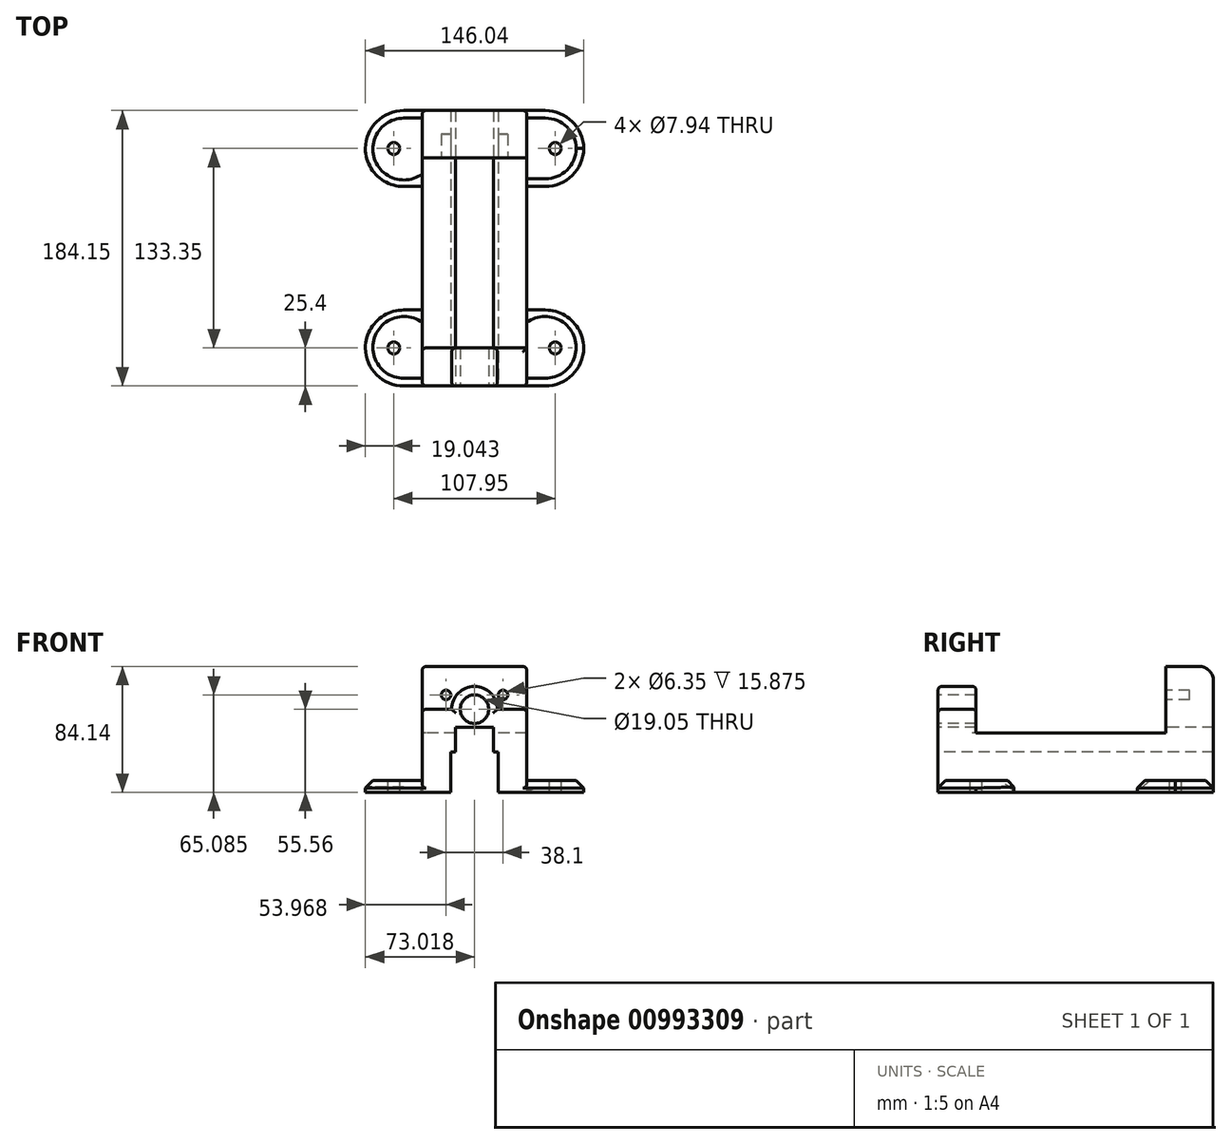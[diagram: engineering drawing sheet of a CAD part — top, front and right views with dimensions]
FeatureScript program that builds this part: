
annotation { "Feature Type Name" : "Feature", "Feature Type Description" : "" }
export const myFeature = defineFeature(function(context is Context, id is Id, definition is map)
    precondition{}
    {
        {
            var Q0;
            Q0=qCreatedBy(makeId("Front.planeOp"),FACE);
            var sketch = newSketch(context, id + "F0", { "sketchPlane" : qUnion([Q0])});
            skLineSegment(sketch, "E0", {"start": v(-29.15, 0) * mm, "end": v(40.7, 0) * mm});
            skLineSegment(sketch, "E1", {"start": v(40.7, 0) * mm, "end": v(40.7, -55.56) * mm});
            skLineSegment(sketch, "E2", {"start": v(40.7, -55.56) * mm, "end": v(-29.15, -55.56) * mm});
            skLineSegment(sketch, "E3", {"start": v(-29.15, -55.56) * mm, "end": v(-29.15, 0) * mm});
            skSolve(sketch);
        }
        {
            var Q0;
            Q0=makeQuery(id+"F0.imprint","IMPRINT",FACE,{"disambiguationData":[TD([[makeQuery(id+"F0.imprint","IMPRINT",EDGE,{"derivedFrom":sQuery(id+"F0.wireOp",EDGE,"E0")}),-1.0]])]});
            extrude(context, id + "F1", {"entities" : qUnion([Q0]), "depth" : 25.4 * mm, "offsetDistance" : 25.4 * mm});
        }
        {
            var Q0;
            Q0=makeQuery(id+"F1.opExtrude","CAP_FACE",FACE,{"disambiguationData":[OSD([sQuery(id+"F0.wireOp",EDGE,"E0"),sQuery(id+"F0.wireOp",EDGE,"E1"),sQuery(id+"F0.wireOp",EDGE,"E2"),sQuery(id+"F0.wireOp",EDGE,"E3")])],"isStart":false});
            var sketch = newSketch(context, id + "F2", { "sketchPlane" : qUnion([Q0])});
            skCircle(sketch, "E4", {"center": v(5.78, 0) * mm, "radius": 15.24 * mm});
            skSolve(sketch);
        }
        {
            var Q0;
            {var subQ0=sQuery(id+"F2.wireOp",EDGE,"E4");var subQ1=makeQuery(id+"F1.opExtrude","CAP_EDGE",EDGE,{"disambiguationData":[OSD([sQuery(id+"F0.wireOp",EDGE,"E0")])],"isStart":false});var subQ2=makeQuery(id+"F2.imprint","INTERSECT",VERTEX,{"disambiguationData":[OD(0.0)],"derivedFrom":[subQ1,subQ0]});Q0=makeQuery(id+"F2.imprint","IMPRINT",FACE,{"disambiguationData":[TD([[makeQuery(id+"F2.imprint","IMPRINT",EDGE,{"disambiguationData":[TD([[subQ2,1.0]])],"derivedFrom":subQ0}),1.0]])]});}
            extrude(context, id + "F3", {"entities" : qUnion([Q0]), "operationType" : NewBodyOperationType.ADD, "oppositeDirection" : true, "depth" : 25.4 * mm, "offsetDistance" : 25.4 * mm});
        }
        {
            var Q0;
            {var subQ0=sQuery(id+"F0.wireOp",EDGE,"E0");Q0=makeQuery(id+"F3.boolean.opBoolean","MERGE",FACE,{"derivedFrom":[makeQuery(id+"F1.opExtrude","CAP_FACE",FACE,{"disambiguationData":[OSD([subQ0,sQuery(id+"F0.wireOp",EDGE,"E1"),sQuery(id+"F0.wireOp",EDGE,"E2"),sQuery(id+"F0.wireOp",EDGE,"E3")])],"isStart":false}),makeQuery(id+"F3.opExtrude","CAP_FACE",FACE,{"disambiguationData":[OSD([subQ0,sQuery(id+"F2.wireOp",EDGE,"E4")])],"isStart":true})]});}
            var sketch = newSketch(context, id + "F4", { "sketchPlane" : qUnion([Q0])});
            skCircle(sketch, "E5", {"center": v(5.78, 0) * mm, "radius": 7.94 * mm});
            skSolve(sketch);
        }
        {
            var Q0;
            Q0=makeQuery(id+"F4.imprint","IMPRINT",FACE,{"disambiguationData":[TD([[makeQuery(id+"F4.imprint","IMPRINT",EDGE,{"derivedFrom":sQuery(id+"F4.wireOp",EDGE,"E5")}),1.0]])]});
            extrude(context, id + "F5", {"entities" : qUnion([Q0]), "operationType" : NewBodyOperationType.REMOVE, "oppositeDirection" : true, "depth" : 25.4 * mm, "offsetDistance" : 25.4 * mm});
        }
        {
            var Q0;
            {var subQ0=sQuery(id+"F0.wireOp",EDGE,"E0");Q0=makeQuery(id+"F3.boolean.opBoolean","MERGE",FACE,{"derivedFrom":[makeQuery(id+"F1.opExtrude","CAP_FACE",FACE,{"disambiguationData":[OSD([subQ0,sQuery(id+"F0.wireOp",EDGE,"E1"),sQuery(id+"F0.wireOp",EDGE,"E2"),sQuery(id+"F0.wireOp",EDGE,"E3")])],"isStart":true}),makeQuery(id+"F3.opExtrude","CAP_FACE",FACE,{"disambiguationData":[OSD([subQ0,sQuery(id+"F2.wireOp",EDGE,"E4")])],"isStart":false})]});}
            var sketch = newSketch(context, id + "F6", { "sketchPlane" : qUnion([Q0])});
            skLineSegment(sketch, "E6", {"start": v(-40.7, -55.56) * mm, "end": v(-40.7, -15.88) * mm});
            skLineSegment(sketch, "E7", {"start": v(-40.7, -15.88) * mm, "end": v(29.15, -15.88) * mm});
            skLineSegment(sketch, "E8", {"start": v(29.15, -15.88) * mm, "end": v(29.15, -55.56) * mm});
            skLineSegment(sketch, "E9", {"start": v(29.15, -55.56) * mm, "end": v(-40.7, -55.56) * mm});
            skSolve(sketch);
        }
        {
            var Q0;
            Q0=makeQuery(id+"F6.imprint","IMPRINT",FACE,{"disambiguationData":[TD([[makeQuery(id+"F6.imprint","IMPRINT",EDGE,{"derivedFrom":sQuery(id+"F6.wireOp",EDGE,"E6")}),1.0]])]});
            extrude(context, id + "F7", {"entities" : qUnion([Q0]), "operationType" : NewBodyOperationType.ADD, "depth" : 127 * mm, "offsetDistance" : 25.4 * mm});
        }
        {
            var Q0;
            Q0=makeQuery(id+"F7.opExtrude","CAP_FACE",FACE,{"disambiguationData":[OSD([sQuery(id+"F6.wireOp",EDGE,"E6"),sQuery(id+"F6.wireOp",EDGE,"E7"),sQuery(id+"F6.wireOp",EDGE,"E8"),sQuery(id+"F6.wireOp",EDGE,"E9")])],"isStart":false});
            var sketch = newSketch(context, id + "F8", { "sketchPlane" : qUnion([Q0])});
            skLineSegment(sketch, "E10", {"start": v(-40.7, -15.88) * mm, "end": v(-40.7, 28.57) * mm});
            skLineSegment(sketch, "E11", {"start": v(-40.7, 28.57) * mm, "end": v(29.15, 28.57) * mm});
            skLineSegment(sketch, "E12", {"start": v(29.15, 28.57) * mm, "end": v(29.15, -15.88) * mm});
            skLineSegment(sketch, "E13", {"start": v(29.15, -15.88) * mm, "end": v(-40.7, -15.88) * mm});
            skSolve(sketch);
        }
        {
            var Q0;
            Q0=makeQuery(id+"F8.imprint","IMPRINT",FACE,{"disambiguationData":[TD([[makeQuery(id+"F8.imprint","IMPRINT",EDGE,{"derivedFrom":sQuery(id+"F8.wireOp",EDGE,"E10")}),-1.0]])]});
            var Q1;
            Q1=makeQuery(id+"F8.imprint","IMPRINT",FACE,{"disambiguationData":[TD([[makeQuery(id+"F8.imprint","IMPRINT",EDGE,{"derivedFrom":sQuery(id+"F8.wireOp",EDGE,"E13")}),-1.0]])]});
            extrude(context, id + "F9", {"entities" : qUnion([Q0, Q1]), "operationType" : NewBodyOperationType.ADD, "depth" : 31.75 * mm, "offsetDistance" : 25.4 * mm});
        }
        {
            var Q0;
            Q0=makeQuery(id+"F9.opExtrude","CAP_EDGE",EDGE,{"disambiguationData":[OSD([sQuery(id+"F8.wireOp",EDGE,"E11")])],"isStart":false});
            fillet(context, id + "F10", {"entities" : qUnion([Q0]), "radius" : 9.52 * mm, "tangentPropagation" : true, "allowEdgeOverflow" : false});
        }
        {
            var Q0;
            {var subQ0=sQuery(id+"F0.wireOp",EDGE,"E0");Q0=makeQuery(id+"F3.boolean.opBoolean","MERGE",FACE,{"derivedFrom":[makeQuery(id+"F1.opExtrude","CAP_FACE",FACE,{"disambiguationData":[OSD([subQ0,sQuery(id+"F0.wireOp",EDGE,"E1"),sQuery(id+"F0.wireOp",EDGE,"E2"),sQuery(id+"F0.wireOp",EDGE,"E3")])],"isStart":false}),makeQuery(id+"F3.opExtrude","CAP_FACE",FACE,{"disambiguationData":[OSD([subQ0,sQuery(id+"F2.wireOp",EDGE,"E4")])],"isStart":true})]});}
            var sketch = newSketch(context, id + "F11", { "sketchPlane" : qUnion([Q0])});
            skLineSegment(sketch, "E14", {"start": v(5.78, -55.56) * mm, "end": v(-10.16, -55.56) * mm});
            skLineSegment(sketch, "E15", {"start": v(-10.16, -55.56) * mm, "end": v(21.72, -55.56) * mm});
            skLineSegment(sketch, "E16", {"start": v(21.72, -55.56) * mm, "end": v(21.72, -28.58) * mm});
            skLineSegment(sketch, "E17", {"start": v(-10.16, -55.56) * mm, "end": v(-10.16, -28.58) * mm});
            skLineSegment(sketch, "E18", {"start": v(-10.16, -28.58) * mm, "end": v(21.72, -28.58) * mm});
            skLineSegment(sketch, "E19", {"start": v(5.78, -28.58) * mm, "end": v(-6.97, -28.58) * mm});
            skLineSegment(sketch, "E20", {"start": v(-6.97, -28.58) * mm, "end": v(18.53, -28.58) * mm});
            skLineSegment(sketch, "E21", {"start": v(18.53, -28.58) * mm, "end": v(18.53, -15.82) * mm});
            skLineSegment(sketch, "E22", {"start": v(-6.97, -28.58) * mm, "end": v(-6.97, -15.82) * mm});
            skLineSegment(sketch, "E23", {"start": v(-6.97, -15.82) * mm, "end": v(18.53, -15.82) * mm});
            skSolve(sketch);
        }
        {
            var Q0;
            {var subQ1=sQuery(id+"F11.wireOp",EDGE,"E21");Q0=makeQuery(id+"F11.imprint","IMPRINT",FACE,{"disambiguationData":[TD([[makeQuery(id+"F11.imprint","IMPRINT",EDGE,{"derivedFrom":subQ1}),1.0]])]});}
            var Q1;
            {var subQ4=sQuery(id+"F11.wireOp",EDGE,"E16");Q1=makeQuery(id+"F11.imprint","IMPRINT",FACE,{"disambiguationData":[TD([[makeQuery(id+"F11.imprint","IMPRINT",EDGE,{"derivedFrom":subQ4}),1.0]])]});}
            extrude(context, id + "F12", {"entities" : qUnion([Q0, Q1]), "operationType" : NewBodyOperationType.REMOVE, "oppositeDirection" : true, "depth" : 210.06 * mm, "offsetDistance" : 25.4 * mm});
        }
        {
            var Q0;
            {var subQ0=sQuery(id+"F0.wireOp",EDGE,"E0");Q0=makeQuery(id+"F3.boolean.opBoolean","MERGE",FACE,{"derivedFrom":[makeQuery(id+"F1.opExtrude","CAP_FACE",FACE,{"disambiguationData":[OSD([subQ0,sQuery(id+"F0.wireOp",EDGE,"E1"),sQuery(id+"F0.wireOp",EDGE,"E2"),sQuery(id+"F0.wireOp",EDGE,"E3")])],"isStart":false}),makeQuery(id+"F3.opExtrude","CAP_FACE",FACE,{"disambiguationData":[OSD([subQ0,sQuery(id+"F2.wireOp",EDGE,"E4")])],"isStart":true})]});}
            var sketch = newSketch(context, id + "F13", { "sketchPlane" : qUnion([Q0])});
            skLineSegment(sketch, "E24", {"start": v(-6.97, -15.82) * mm, "end": v(-6.97, -12.01) * mm});
            skLineSegment(sketch, "E25", {"start": v(-6.97, -12.01) * mm, "end": v(18.53, -12.01) * mm});
            skLineSegment(sketch, "E26", {"start": v(18.53, -12.01) * mm, "end": v(18.53, -15.82) * mm});
            skSolve(sketch);
        }
        {
            var Q0;
            Q0=makeQuery(id+"F13.imprint","IMPRINT",FACE,{"disambiguationData":[TD([[makeQuery(id+"F13.imprint","IMPRINT",EDGE,{"derivedFrom":sQuery(id+"F13.wireOp",EDGE,"E24")}),-1.0]])]});
            extrude(context, id + "F14", {"entities" : qUnion([Q0]), "operationType" : NewBodyOperationType.REMOVE, "oppositeDirection" : true, "depth" : 222 * mm, "offsetDistance" : 25.4 * mm});
        }
        {
            var Q0;
            Q0=makeQuery(id+"F9.opExtrude","CAP_FACE",FACE,{"disambiguationData":[OSD([sQuery(id+"F6.wireOp",EDGE,"E6"),sQuery(id+"F6.wireOp",EDGE,"E8"),sQuery(id+"F6.wireOp",EDGE,"E9"),sQuery(id+"F8.wireOp",EDGE,"E10"),sQuery(id+"F8.wireOp",EDGE,"E11"),sQuery(id+"F8.wireOp",EDGE,"E12")])],"isStart":true});
            var sketch = newSketch(context, id + "F15", { "sketchPlane" : qUnion([Q0])});
            skLineSegment(sketch, "E27", {"start": v(-29.15, 28.57) * mm, "end": v(-29.15, 9.52) * mm});
            skLineSegment(sketch, "E28", {"start": v(-29.15, 9.52) * mm, "end": v(-13.27, 9.52) * mm});
            skCircle(sketch, "E29", {"center": v(-13.27, 9.52) * mm, "radius": 3.18 * mm});
            skLineSegment(sketch, "E30", {"start": v(40.7, 28.57) * mm, "end": v(40.7, 9.52) * mm});
            skLineSegment(sketch, "E31", {"start": v(40.7, 9.52) * mm, "end": v(24.83, 9.52) * mm});
            skCircle(sketch, "E32", {"center": v(24.83, 9.52) * mm, "radius": 3.18 * mm});
            skSolve(sketch);
        }
        {
            var Q0;
            Q0=makeQuery(id+"F15.imprint","IMPRINT",FACE,{"disambiguationData":[TD([[makeQuery(id+"F15.imprint","IMPRINT",EDGE,{"derivedFrom":sQuery(id+"F15.wireOp",EDGE,"E29")}),1.0]])]});
            var Q1;
            Q1=makeQuery(id+"F15.imprint","IMPRINT",FACE,{"disambiguationData":[TD([[makeQuery(id+"F15.imprint","IMPRINT",EDGE,{"derivedFrom":sQuery(id+"F15.wireOp",EDGE,"E32")}),1.0]])]});
            extrude(context, id + "F16", {"entities" : qUnion([Q0, Q1]), "operationType" : NewBodyOperationType.REMOVE, "oppositeDirection" : true, "depth" : 15.88 * mm, "offsetDistance" : 25.4 * mm});
        }
        {
            var Q0;
            {var subQ0=sQuery(id+"F6.wireOp",EDGE,"E6");Q0=makeQuery(id+"F9.boolean.opBoolean","MERGE",FACE,{"derivedFrom":[makeQuery(id+"F7.boolean.opBoolean","MERGE",FACE,{"derivedFrom":[makeQuery(id+"F1.opExtrude","SWEPT_FACE",FACE,{"disambiguationData":[OSD([sQuery(id+"F0.wireOp",EDGE,"E1")])]}),makeQuery(id+"F7.opExtrude","SWEPT_FACE",FACE,{"disambiguationData":[OSD([subQ0])]})]}),makeQuery(id+"F9.opExtrude","SWEPT_FACE",FACE,{"disambiguationData":[OSD([subQ0,sQuery(id+"F8.wireOp",EDGE,"E10")])]})]});}
            var sketch = newSketch(context, id + "F17", { "sketchPlane" : qUnion([Q0])});
            skLineSegment(sketch, "E33", {"start": v(-25.4, -55.56) * mm, "end": v(-25.4, -47.63) * mm});
            skLineSegment(sketch, "E34", {"start": v(-25.4, -47.63) * mm, "end": v(25.4, -47.63) * mm});
            skLineSegment(sketch, "E35", {"start": v(25.4, -47.63) * mm, "end": v(25.4, -55.56) * mm});
            skLineSegment(sketch, "E36", {"start": v(25.4, -55.56) * mm, "end": v(-25.4, -55.56) * mm});
            skLineSegment(sketch, "E37", {"start": v(158.75, -55.56) * mm, "end": v(158.75, -47.63) * mm});
            skLineSegment(sketch, "E38", {"start": v(158.75, -47.63) * mm, "end": v(107.95, -47.63) * mm});
            skLineSegment(sketch, "E39", {"start": v(107.95, -47.63) * mm, "end": v(107.95, -55.56) * mm});
            skLineSegment(sketch, "E40", {"start": v(107.95, -55.56) * mm, "end": v(158.75, -55.56) * mm});
            skSolve(sketch);
        }
        {
            var Q0;
            Q0=makeQuery(id+"F17.imprint","IMPRINT",FACE,{"disambiguationData":[TD([[makeQuery(id+"F17.imprint","IMPRINT",EDGE,{"derivedFrom":sQuery(id+"F17.wireOp",EDGE,"E33")}),1.0]])]});
            var Q1;
            Q1=makeQuery(id+"F17.imprint","IMPRINT",FACE,{"disambiguationData":[TD([[makeQuery(id+"F17.imprint","IMPRINT",EDGE,{"derivedFrom":sQuery(id+"F17.wireOp",EDGE,"E37")}),1.0]])]});
            extrude(context, id + "F18", {"entities" : qUnion([Q0, Q1]), "operationType" : NewBodyOperationType.ADD, "depth" : 38.1 * mm, "offsetDistance" : 25.4 * mm});
        }
        {
            var Q0;
            {var subQ0=sQuery(id+"F6.wireOp",EDGE,"E8");Q0=makeQuery(id+"F9.boolean.opBoolean","MERGE",FACE,{"derivedFrom":[makeQuery(id+"F7.boolean.opBoolean","MERGE",FACE,{"derivedFrom":[makeQuery(id+"F1.opExtrude","SWEPT_FACE",FACE,{"disambiguationData":[OSD([sQuery(id+"F0.wireOp",EDGE,"E3")])]}),makeQuery(id+"F7.opExtrude","SWEPT_FACE",FACE,{"disambiguationData":[OSD([subQ0])]})]}),makeQuery(id+"F9.opExtrude","SWEPT_FACE",FACE,{"disambiguationData":[OSD([subQ0,sQuery(id+"F8.wireOp",EDGE,"E12")])]})]});}
            var sketch = newSketch(context, id + "F19", { "sketchPlane" : qUnion([Q0])});
            skLineSegment(sketch, "E41", {"start": v(25.4, -55.56) * mm, "end": v(25.4, -47.63) * mm});
            skLineSegment(sketch, "E42", {"start": v(25.4, -47.63) * mm, "end": v(-25.4, -47.63) * mm});
            skLineSegment(sketch, "E43", {"start": v(-25.4, -47.63) * mm, "end": v(-25.4, -55.56) * mm});
            skLineSegment(sketch, "E44", {"start": v(-25.4, -55.56) * mm, "end": v(25.4, -55.56) * mm});
            skLineSegment(sketch, "E45", {"start": v(-158.75, -55.56) * mm, "end": v(-158.75, -47.63) * mm});
            skLineSegment(sketch, "E46", {"start": v(-158.75, -47.63) * mm, "end": v(-107.95, -47.63) * mm});
            skLineSegment(sketch, "E47", {"start": v(-107.95, -47.63) * mm, "end": v(-107.95, -55.56) * mm});
            skLineSegment(sketch, "E48", {"start": v(-107.95, -55.56) * mm, "end": v(-158.75, -55.56) * mm});
            skSolve(sketch);
        }
        {
            var Q0;
            Q0=makeQuery(id+"F19.imprint","IMPRINT",FACE,{"disambiguationData":[TD([[makeQuery(id+"F19.imprint","IMPRINT",EDGE,{"derivedFrom":sQuery(id+"F19.wireOp",EDGE,"E45")}),1.0]])]});
            var Q1;
            Q1=makeQuery(id+"F19.imprint","IMPRINT",FACE,{"disambiguationData":[TD([[makeQuery(id+"F19.imprint","IMPRINT",EDGE,{"derivedFrom":sQuery(id+"F19.wireOp",EDGE,"E41")}),1.0]])]});
            extrude(context, id + "F20", {"entities" : qUnion([Q0, Q1]), "operationType" : NewBodyOperationType.ADD, "depth" : 38.1 * mm, "offsetDistance" : 25.4 * mm});
        }
        {
            var Q0;
            Q0=makeQuery(id+"F18.opExtrude","SWEPT_FACE",FACE,{"disambiguationData":[OSD([sQuery(id+"F17.wireOp",EDGE,"E34")])]});
            var sketch = newSketch(context, id + "F21", { "sketchPlane" : qUnion([Q0])});
            skLineSegment(sketch, "E49", {"start": v(59.75, -25.4) * mm, "end": v(59.75, 0) * mm});
            skCircle(sketch, "E50", {"center": v(59.75, 0) * mm, "radius": 3.97 * mm});
            skSolve(sketch);
        }
        {
            var Q0;
            Q0=makeQuery(id+"F18.opExtrude","SWEPT_FACE",FACE,{"disambiguationData":[OSD([sQuery(id+"F17.wireOp",EDGE,"E38")])]});
            var sketch = newSketch(context, id + "F22", { "sketchPlane" : qUnion([Q0])});
            skLineSegment(sketch, "E51", {"start": v(59.75, 107.95) * mm, "end": v(59.75, 133.35) * mm});
            skCircle(sketch, "E52", {"center": v(59.75, 133.35) * mm, "radius": 3.97 * mm});
            skSolve(sketch);
        }
        {
            var Q0;
            Q0=makeQuery(id+"F20.opExtrude","SWEPT_FACE",FACE,{"disambiguationData":[OSD([sQuery(id+"F19.wireOp",EDGE,"E46")])]});
            var sketch = newSketch(context, id + "F23", { "sketchPlane" : qUnion([Q0])});
            skLineSegment(sketch, "E53", {"start": v(-48.2, 107.95) * mm, "end": v(-48.2, 133.35) * mm});
            skCircle(sketch, "E54", {"center": v(-48.2, 133.35) * mm, "radius": 3.97 * mm});
            skSolve(sketch);
        }
        {
            var Q0;
            Q0=makeQuery(id+"F20.opExtrude","SWEPT_FACE",FACE,{"disambiguationData":[OSD([sQuery(id+"F19.wireOp",EDGE,"E42")])]});
            var sketch = newSketch(context, id + "F24", { "sketchPlane" : qUnion([Q0])});
            skLineSegment(sketch, "E55", {"start": v(-48.2, 25.4) * mm, "end": v(-48.2, 0) * mm});
            skCircle(sketch, "E56", {"center": v(-48.2, 0) * mm, "radius": 3.97 * mm});
            skSolve(sketch);
        }
        {
            var Q0;
            Q0=makeQuery(id+"F23.imprint","IMPRINT",FACE,{"disambiguationData":[TD([[makeQuery(id+"F23.imprint","IMPRINT",EDGE,{"derivedFrom":sQuery(id+"F23.wireOp",EDGE,"E54")}),1.0]])]});
            var Q1;
            Q1=makeQuery(id+"F22.imprint","IMPRINT",FACE,{"disambiguationData":[TD([[makeQuery(id+"F22.imprint","IMPRINT",EDGE,{"derivedFrom":sQuery(id+"F22.wireOp",EDGE,"E52")}),1.0]])]});
            var Q2;
            Q2=makeQuery(id+"F21.imprint","IMPRINT",FACE,{"disambiguationData":[TD([[makeQuery(id+"F21.imprint","IMPRINT",EDGE,{"derivedFrom":sQuery(id+"F21.wireOp",EDGE,"E50")}),1.0]])]});
            var Q3;
            Q3=makeQuery(id+"F24.imprint","IMPRINT",FACE,{"disambiguationData":[TD([[makeQuery(id+"F24.imprint","IMPRINT",EDGE,{"derivedFrom":sQuery(id+"F24.wireOp",EDGE,"E56")}),1.0]])]});
            extrude(context, id + "F25", {"entities" : qUnion([Q0, Q1, Q2, Q3]), "operationType" : NewBodyOperationType.REMOVE, "oppositeDirection" : true, "depth" : 25.4 * mm, "offsetDistance" : 25.4 * mm});
        }
        {
            var Q0;
            Q0=makeQuery(id+"F18.opExtrude","CAP_EDGE",EDGE,{"disambiguationData":[OSD([sQuery(id+"F17.wireOp",EDGE,"E33")])],"isStart":false});
            var Q1;
            Q1=makeQuery(id+"F18.opExtrude","CAP_EDGE",EDGE,{"disambiguationData":[OSD([sQuery(id+"F17.wireOp",EDGE,"E35")])],"isStart":false});
            var Q2;
            Q2=makeQuery(id+"F18.opExtrude","CAP_EDGE",EDGE,{"disambiguationData":[OSD([sQuery(id+"F17.wireOp",EDGE,"E39")])],"isStart":false});
            var Q3;
            Q3=makeQuery(id+"F18.opExtrude","CAP_EDGE",EDGE,{"disambiguationData":[OSD([sQuery(id+"F17.wireOp",EDGE,"E37")])],"isStart":false});
            var Q4;
            Q4=makeQuery(id+"F20.opExtrude","CAP_EDGE",EDGE,{"disambiguationData":[OSD([sQuery(id+"F19.wireOp",EDGE,"E43")])],"isStart":false});
            var Q5;
            Q5=makeQuery(id+"F20.opExtrude","CAP_EDGE",EDGE,{"disambiguationData":[OSD([sQuery(id+"F19.wireOp",EDGE,"E41")])],"isStart":false});
            var Q6;
            Q6=makeQuery(id+"F20.opExtrude","CAP_EDGE",EDGE,{"disambiguationData":[OSD([sQuery(id+"F19.wireOp",EDGE,"E47")])],"isStart":false});
            var Q7;
            Q7=makeQuery(id+"F20.opExtrude","CAP_EDGE",EDGE,{"disambiguationData":[OSD([sQuery(id+"F19.wireOp",EDGE,"E45")])],"isStart":false});
            fillet(context, id + "F26", {"entities" : qUnion([Q0, Q1, Q2, Q3, Q4, Q5, Q6, Q7]), "radius" : 25.75 * mm, "tangentPropagation" : true, "allowEdgeOverflow" : false});
        }
        {
            var Q0;
            Q0=makeQuery(id+"F1.opExtrude","SWEPT_EDGE",EDGE,{"disambiguationData":[OSD([sQuery(id+"F0.wireOp",EDGE,"E0"),sQuery(id+"F0.wireOp",EDGE,"E3")])]});
            var Q1;
            Q1=makeQuery(id+"F1.opExtrude","CAP_EDGE",EDGE,{"disambiguationData":[OSD([sQuery(id+"F0.wireOp",EDGE,"E3")])],"isStart":false});
            var Q2;
            {var subQ1=sQuery(id+"F0.wireOp",EDGE,"E3");var subQ2=sQuery(id+"F0.wireOp",EDGE,"E0");Q2=makeQuery(id+"F3.boolean.opBoolean","SPLIT",EDGE,{"disambiguationData":[TD([makeQuery(id+"F1.opExtrude","SWEPT_FACE",FACE,{"disambiguationData":[OSD([subQ1])]})])],"derivedFrom":makeQuery(id+"F1.opExtrude","CAP_EDGE",EDGE,{"disambiguationData":[OSD([subQ2])],"isStart":false})});}
            var Q3;
            {var subQ1=sQuery(id+"F0.wireOp",EDGE,"E3");var subQ2=sQuery(id+"F0.wireOp",EDGE,"E0");Q3=makeQuery(id+"F3.boolean.opBoolean","SPLIT",EDGE,{"disambiguationData":[TD([makeQuery(id+"F1.opExtrude","SWEPT_FACE",FACE,{"disambiguationData":[OSD([subQ1])]})])],"derivedFrom":makeQuery(id+"F1.opExtrude","CAP_EDGE",EDGE,{"disambiguationData":[OSD([subQ2])],"isStart":true})});}
            var Q4;
            Q4=makeQuery(id+"F3.opExtrude","CAP_EDGE",EDGE,{"disambiguationData":[OSD([sQuery(id+"F2.wireOp",EDGE,"E4")])],"isStart":true});
            var Q5;
            {var subQ1=sQuery(id+"F0.wireOp",EDGE,"E1");var subQ2=sQuery(id+"F0.wireOp",EDGE,"E0");Q5=makeQuery(id+"F3.boolean.opBoolean","SPLIT",EDGE,{"disambiguationData":[TD([makeQuery(id+"F1.opExtrude","SWEPT_FACE",FACE,{"disambiguationData":[OSD([subQ1])]})])],"derivedFrom":makeQuery(id+"F1.opExtrude","CAP_EDGE",EDGE,{"disambiguationData":[OSD([subQ2])],"isStart":false})});}
            var Q6;
            Q6=makeQuery(id+"F1.opExtrude","SWEPT_EDGE",EDGE,{"disambiguationData":[OSD([sQuery(id+"F0.wireOp",EDGE,"E0"),sQuery(id+"F0.wireOp",EDGE,"E1")])]});
            var Q7;
            {var subQ1=sQuery(id+"F0.wireOp",EDGE,"E1");var subQ2=sQuery(id+"F0.wireOp",EDGE,"E0");Q7=makeQuery(id+"F3.boolean.opBoolean","SPLIT",EDGE,{"disambiguationData":[TD([makeQuery(id+"F1.opExtrude","SWEPT_FACE",FACE,{"disambiguationData":[OSD([subQ1])]})])],"derivedFrom":makeQuery(id+"F1.opExtrude","CAP_EDGE",EDGE,{"disambiguationData":[OSD([subQ2])],"isStart":true})});}
            var Q8;
            Q8=makeQuery(id+"F3.opExtrude","CAP_EDGE",EDGE,{"disambiguationData":[OSD([sQuery(id+"F2.wireOp",EDGE,"E4")])],"isStart":false});
            var Q9;
            Q9=makeQuery(id+"F1.opExtrude","CAP_EDGE",EDGE,{"disambiguationData":[OSD([sQuery(id+"F0.wireOp",EDGE,"E1")])],"isStart":false});
            var Q10;
            Q10=makeQuery(id+"F1.opExtrude","CAP_EDGE",EDGE,{"disambiguationData":[OSD([sQuery(id+"F0.wireOp",EDGE,"E3")])],"isStart":true});
            var Q11;
            {var subQ0=sQuery(id+"F6.wireOp",EDGE,"E8");Q11=makeQuery(id+"F10.opFillet","BLEND_EDGE",EDGE,{"blendedFrom":[makeQuery(id+"F9.opExtrude","CAP_EDGE",EDGE,{"disambiguationData":[OSD([sQuery(id+"F8.wireOp",EDGE,"E11")])],"isStart":false}),makeQuery(id+"F9.boolean.opBoolean","MERGE",FACE,{"derivedFrom":[makeQuery(id+"F7.boolean.opBoolean","MERGE",FACE,{"derivedFrom":[makeQuery(id+"F1.opExtrude","SWEPT_FACE",FACE,{"disambiguationData":[OSD([sQuery(id+"F0.wireOp",EDGE,"E3")])]}),makeQuery(id+"F7.opExtrude","SWEPT_FACE",FACE,{"disambiguationData":[OSD([subQ0])]})]}),makeQuery(id+"F9.opExtrude","SWEPT_FACE",FACE,{"disambiguationData":[OSD([subQ0,sQuery(id+"F8.wireOp",EDGE,"E12")])]})]})],"blendedInto":[makeQuery(id+"F9.boolean.opBoolean","MERGE",FACE,{"derivedFrom":[makeQuery(id+"F7.boolean.opBoolean","MERGE",FACE,{"derivedFrom":[makeQuery(id+"F1.opExtrude","SWEPT_FACE",FACE,{"disambiguationData":[OSD([sQuery(id+"F0.wireOp",EDGE,"E3")])]}),makeQuery(id+"F7.opExtrude","SWEPT_FACE",FACE,{"disambiguationData":[OSD([subQ0])]})]}),makeQuery(id+"F9.opExtrude","SWEPT_FACE",FACE,{"disambiguationData":[OSD([subQ0,sQuery(id+"F8.wireOp",EDGE,"E12")])]})]})]});}
            var Q12;
            Q12=makeQuery(id+"F9.opExtrude","SWEPT_EDGE",EDGE,{"disambiguationData":[OSD([sQuery(id+"F8.wireOp",EDGE,"E10"),sQuery(id+"F8.wireOp",EDGE,"E11")])]});
            fillet(context, id + "F27", {"entities" : qUnion([Q0, Q1, Q2, Q3, Q4, Q5, Q6, Q7, Q8, Q9, Q10, Q11, Q12]), "radius" : 2.54 * mm, "tangentPropagation" : true, "allowEdgeOverflow" : false});
        }
        {
            var Q0;
            Q0=makeQuery(id+"F26.opFillet","BLEND_EDGE",EDGE,{"blendedFrom":[makeQuery(id+"F18.opExtrude","CAP_EDGE",EDGE,{"disambiguationData":[OSD([sQuery(id+"F17.wireOp",EDGE,"E33")])],"isStart":false}),makeQuery(id+"F18.opExtrude","SWEPT_FACE",FACE,{"disambiguationData":[OSD([sQuery(id+"F17.wireOp",EDGE,"E34")])]})],"blendedInto":[makeQuery(id+"F18.opExtrude","SWEPT_FACE",FACE,{"disambiguationData":[OSD([sQuery(id+"F17.wireOp",EDGE,"E34")])]})]});
            chamfer(context, id + "F28", {"entities" : qUnion([Q0]), "width" : 5.08 * mm, "tangentPropagation" : true});
        }
        {
            var Q0;
            Q0=makeQuery(id+"F26.opFillet","BLEND_EDGE",EDGE,{"blendedFrom":[makeQuery(id+"F18.opExtrude","CAP_EDGE",EDGE,{"disambiguationData":[OSD([sQuery(id+"F17.wireOp",EDGE,"E39")])],"isStart":false}),makeQuery(id+"F18.opExtrude","SWEPT_FACE",FACE,{"disambiguationData":[OSD([sQuery(id+"F17.wireOp",EDGE,"E38")])]})],"blendedInto":[makeQuery(id+"F18.opExtrude","SWEPT_FACE",FACE,{"disambiguationData":[OSD([sQuery(id+"F17.wireOp",EDGE,"E38")])]})]});
            var Q1;
            Q1=makeQuery(id+"F26.opFillet","BLEND_EDGE",EDGE,{"blendedFrom":[makeQuery(id+"F18.opExtrude","CAP_EDGE",EDGE,{"disambiguationData":[OSD([sQuery(id+"F17.wireOp",EDGE,"E37")])],"isStart":false}),makeQuery(id+"F18.opExtrude","SWEPT_FACE",FACE,{"disambiguationData":[OSD([sQuery(id+"F17.wireOp",EDGE,"E38")])]})],"blendedInto":[makeQuery(id+"F18.opExtrude","SWEPT_FACE",FACE,{"disambiguationData":[OSD([sQuery(id+"F17.wireOp",EDGE,"E38")])]})]});
            chamfer(context, id + "F29", {"entities" : qUnion([Q0, Q1]), "width" : 5.08 * mm, "tangentPropagation" : true});
        }
        {
            var Q0;
            Q0=makeQuery(id+"F26.opFillet","BLEND_EDGE",EDGE,{"blendedFrom":[makeQuery(id+"F20.opExtrude","CAP_EDGE",EDGE,{"disambiguationData":[OSD([sQuery(id+"F19.wireOp",EDGE,"E45")])],"isStart":false}),makeQuery(id+"F20.opExtrude","SWEPT_FACE",FACE,{"disambiguationData":[OSD([sQuery(id+"F19.wireOp",EDGE,"E46")])]})],"blendedInto":[makeQuery(id+"F20.opExtrude","SWEPT_FACE",FACE,{"disambiguationData":[OSD([sQuery(id+"F19.wireOp",EDGE,"E46")])]})]});
            var Q1;
            Q1=makeQuery(id+"F26.opFillet","BLEND_EDGE",EDGE,{"blendedFrom":[makeQuery(id+"F20.opExtrude","CAP_EDGE",EDGE,{"disambiguationData":[OSD([sQuery(id+"F19.wireOp",EDGE,"E41")])],"isStart":false}),makeQuery(id+"F20.opExtrude","SWEPT_FACE",FACE,{"disambiguationData":[OSD([sQuery(id+"F19.wireOp",EDGE,"E42")])]})],"blendedInto":[makeQuery(id+"F20.opExtrude","SWEPT_FACE",FACE,{"disambiguationData":[OSD([sQuery(id+"F19.wireOp",EDGE,"E42")])]})]});
            chamfer(context, id + "F30", {"entities" : qUnion([Q0, Q1]), "width" : 5.08 * mm, "tangentPropagation" : true});
        }
        {
            var Q0;
            {var subQ0=sQuery(id+"F0.wireOp",EDGE,"E0");Q0=makeQuery(id+"F20.boolean.opBoolean","MERGE",FACE,{"derivedFrom":[makeQuery(id+"F18.boolean.opBoolean","MERGE",FACE,{"derivedFrom":[makeQuery(id+"F3.boolean.opBoolean","MERGE",FACE,{"derivedFrom":[makeQuery(id+"F1.opExtrude","CAP_FACE",FACE,{"disambiguationData":[OSD([subQ0,sQuery(id+"F0.wireOp",EDGE,"E1"),sQuery(id+"F0.wireOp",EDGE,"E2"),sQuery(id+"F0.wireOp",EDGE,"E3")])],"isStart":false}),makeQuery(id+"F3.opExtrude","CAP_FACE",FACE,{"disambiguationData":[OSD([subQ0,sQuery(id+"F2.wireOp",EDGE,"E4")])],"isStart":true})]}),makeQuery(id+"F18.opExtrude","SWEPT_FACE",FACE,{"disambiguationData":[OSD([sQuery(id+"F17.wireOp",EDGE,"E33")])]})]}),makeQuery(id+"F20.opExtrude","SWEPT_FACE",FACE,{"disambiguationData":[OSD([sQuery(id+"F19.wireOp",EDGE,"E41")])]})]});}
            var sketch = newSketch(context, id + "F31", { "sketchPlane" : qUnion([Q0])});
            skCircle(sketch, "E57", {"center": v(5.78, 0) * mm, "radius": 9.53 * mm});
            skSolve(sketch);
        }
        {
            var Q0;
            Q0=makeQuery(id+"F31.imprint","IMPRINT",FACE,{"disambiguationData":[TD([[makeQuery(id+"F31.imprint","IMPRINT",EDGE,{"derivedFrom":sQuery(id+"F31.wireOp",EDGE,"E57")}),1.0]])]});
            extrude(context, id + "F32", {"entities" : qUnion([Q0]), "operationType" : NewBodyOperationType.REMOVE, "oppositeDirection" : true, "depth" : 25.4 * mm, "offsetDistance" : 25.4 * mm});
        }
    });
